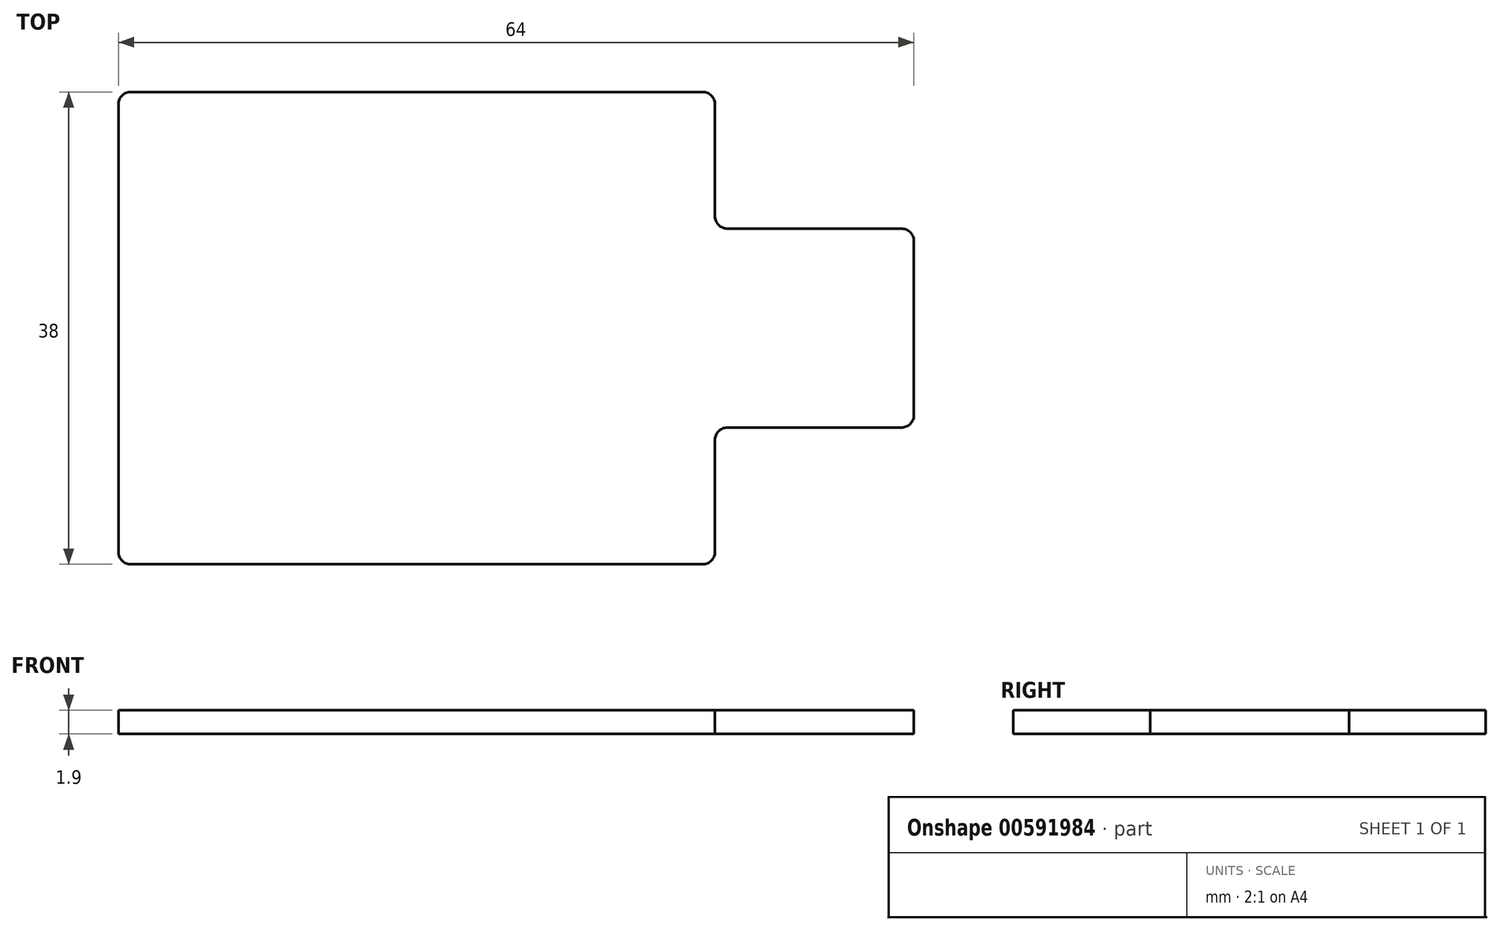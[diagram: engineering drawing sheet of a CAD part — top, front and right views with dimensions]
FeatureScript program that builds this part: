
annotation { "Feature Type Name" : "Feature", "Feature Type Description" : "" }
export const myFeature = defineFeature(function(context is Context, id is Id, definition is map)
    precondition{}
    {
        {
            var Q0;
            Q0=qCreatedBy(makeId("Top.planeOp"),FACE);
            var sketch = newSketch(context, id + "F0", { "sketchPlane" : qUnion([Q0])});
            skLineSegment(sketch, "E0.bottom", {"start": v(-32, -19) * mm, "end": v(16, -19) * mm});
            skLineSegment(sketch, "E0.top", {"start": v(-32, 19) * mm, "end": v(16, 19) * mm});
            skLineSegment(sketch, "E0.left", {"start": v(-32, -19) * mm, "end": v(-32, 19) * mm});
            skLineSegment(sketch, "E0.right", {"start": v(32, -8) * mm, "end": v(32, 8) * mm});
            skPoint(sketch, "E0.middle", {"position": v(0, 0) * mm});
            skLineSegment(sketch, "E1", {"start": v(16, 19) * mm, "end": v(16, 8) * mm});
            skLineSegment(sketch, "E2.top", {"start": v(32, 8) * mm, "end": v(16, 8) * mm});
            skLineSegment(sketch, "E3.top", {"start": v(32, -8) * mm, "end": v(16, -8) * mm});
            skLineSegment(sketch, "E3.right", {"start": v(16, -19) * mm, "end": v(16, -8) * mm});
            skPoint(sketch, "E4.orphan", {"position": v(32, 19) * mm});
            skPoint(sketch, "E5.orphan", {"position": v(32, -19) * mm});
            skLineSegment(sketch, "E6.trimOffspring", {"start": v(16, -8) * mm, "end": v(16, -19) * mm});
            skSolve(sketch);
        }
        {
            var Q0;
            Q0 = qSketchRegion(id + "F0", true);
            extrude(context, id + "F1", {"entities" : qUnion([Q0]), "depth" : 1.9 * mm, "offsetDistance" : 25 * mm});
        }
        {
            var Q0;
            Q0=makeQuery(id+"F1.opExtrude","SWEPT_EDGE",EDGE,{"disambiguationData":[OSD([sQuery(id+"F0.wireOp",EDGE,"E0.bottom"),sQuery(id+"F0.wireOp",EDGE,"E6.trimOffspring")])]});
            var Q1;
            Q1=makeQuery(id+"F1.opExtrude","SWEPT_EDGE",EDGE,{"disambiguationData":[OSD([sQuery(id+"F0.wireOp",EDGE,"E0.bottom"),sQuery(id+"F0.wireOp",EDGE,"E0.left")])]});
            var Q2;
            Q2=makeQuery(id+"F1.opExtrude","SWEPT_EDGE",EDGE,{"disambiguationData":[OSD([sQuery(id+"F0.wireOp",EDGE,"E0.top"),sQuery(id+"F0.wireOp",EDGE,"E0.left")])]});
            var Q3;
            Q3=makeQuery(id+"F1.opExtrude","SWEPT_EDGE",EDGE,{"disambiguationData":[OSD([sQuery(id+"F0.wireOp",EDGE,"E0.top"),sQuery(id+"F0.wireOp",EDGE,"E1")])]});
            var Q4;
            Q4=makeQuery(id+"F1.opExtrude","SWEPT_EDGE",EDGE,{"disambiguationData":[OSD([sQuery(id+"F0.wireOp",EDGE,"E0.right"),sQuery(id+"F0.wireOp",EDGE,"E2.top")])]});
            var Q5;
            Q5=makeQuery(id+"F1.opExtrude","SWEPT_EDGE",EDGE,{"disambiguationData":[OSD([sQuery(id+"F0.wireOp",EDGE,"E0.right"),sQuery(id+"F0.wireOp",EDGE,"E3.top")])]});
            var Q6;
            Q6=makeQuery(id+"F1.opExtrude","SWEPT_EDGE",EDGE,{"disambiguationData":[OSD([sQuery(id+"F0.wireOp",EDGE,"E3.top"),sQuery(id+"F0.wireOp",EDGE,"E6.trimOffspring")])]});
            var Q7;
            Q7=makeQuery(id+"F1.opExtrude","SWEPT_EDGE",EDGE,{"disambiguationData":[OSD([sQuery(id+"F0.wireOp",EDGE,"E2.top"),sQuery(id+"F0.wireOp",EDGE,"E1")])]});
            fillet(context, id + "F2", {"entities" : qUnion([Q0, Q1, Q2, Q3, Q4, Q5, Q6, Q7]), "radius" : 1 * mm, "tangentPropagation" : true, "allowEdgeOverflow" : false});
        }
    });
